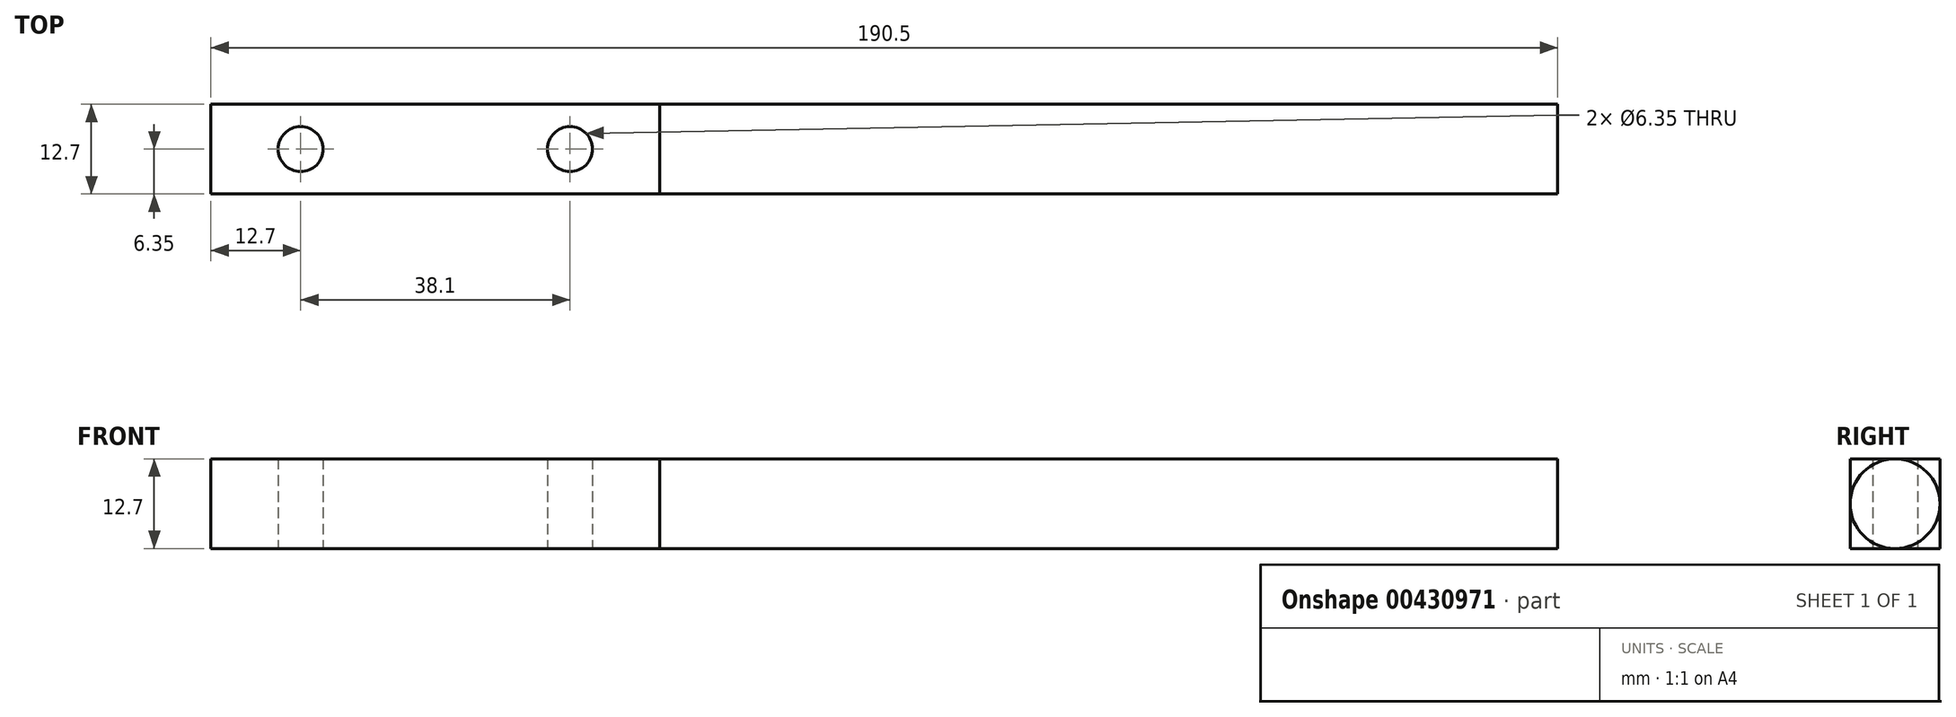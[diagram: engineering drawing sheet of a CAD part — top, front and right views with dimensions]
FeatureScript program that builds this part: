
annotation { "Feature Type Name" : "Feature", "Feature Type Description" : "" }
export const myFeature = defineFeature(function(context is Context, id is Id, definition is map)
    precondition{}
    {
        {
            var Q0;
            Q0=qCreatedBy(makeId("Top.planeOp"),FACE);
            var sketch = newSketch(context, id + "F0", { "sketchPlane" : qUnion([Q0])});
            skLineSegment(sketch, "E0.bottom", {"start": v(-63.5, 6.35) * mm, "end": v(0, 6.35) * mm});
            skLineSegment(sketch, "E0.top", {"start": v(-63.5, -6.35) * mm, "end": v(0, -6.35) * mm});
            skLineSegment(sketch, "E0.left", {"start": v(-63.5, 6.35) * mm, "end": v(-63.5, -6.35) * mm});
            skLineSegment(sketch, "E0.right", {"start": v(0, 6.35) * mm, "end": v(0, -6.35) * mm});
            skPoint(sketch, "E1.positionSnap0", {"position": v(0, 0) * mm});
            skCircle(sketch, "E2", {"center": v(-50.8, 0) * mm, "radius": 3.18 * mm});
            skCircle(sketch, "E3", {"center": v(-12.7, 0) * mm, "radius": 3.18 * mm});
            skSolve(sketch);
        }
        {
            var Q0;
            Q0 = qSketchRegion(id + "F0", true);
            extrude(context, id + "F1", {"entities" : qUnion([Q0]), "endBound" : BoundingType.SYMMETRIC, "depth" : 12.7 * mm});
        }
        {
            var Q0;
            Q0=qCreatedBy(makeId("Top.planeOp"),FACE);
            var sketch = newSketch(context, id + "F2", { "sketchPlane" : qUnion([Q0])});
            skLineSegment(sketch, "E4.bottom", {"start": v(0, 0) * mm, "end": v(127, 0) * mm});
            skLineSegment(sketch, "E4.top", {"start": v(0, 6.35) * mm, "end": v(127, 6.35) * mm});
            skLineSegment(sketch, "E4.left", {"start": v(0, 0) * mm, "end": v(0, 6.35) * mm});
            skLineSegment(sketch, "E4.right", {"start": v(127, 0) * mm, "end": v(127, 6.35) * mm});
            skSolve(sketch);
        }
        {
            var Q0;
            Q0=makeQuery(id+"F2.imprint","IMPRINT",FACE,{"disambiguationData":[TD([[makeQuery(id+"F2.imprint","IMPRINT",EDGE,{"derivedFrom":sQuery(id+"F2.wireOp",EDGE,"E4.bottom")}),1.0]])]});
            var Q1;
            Q1=sQuery(id+"F2.wireOp",EDGE,"E4.bottom");
            revolve(context, id + "F3", {"operationType" : NewBodyOperationType.ADD, "entities" : qUnion([Q0]), "axis" : qUnion([Q1]), "revolveType" : RevolveType.FULL});
        }
    });
